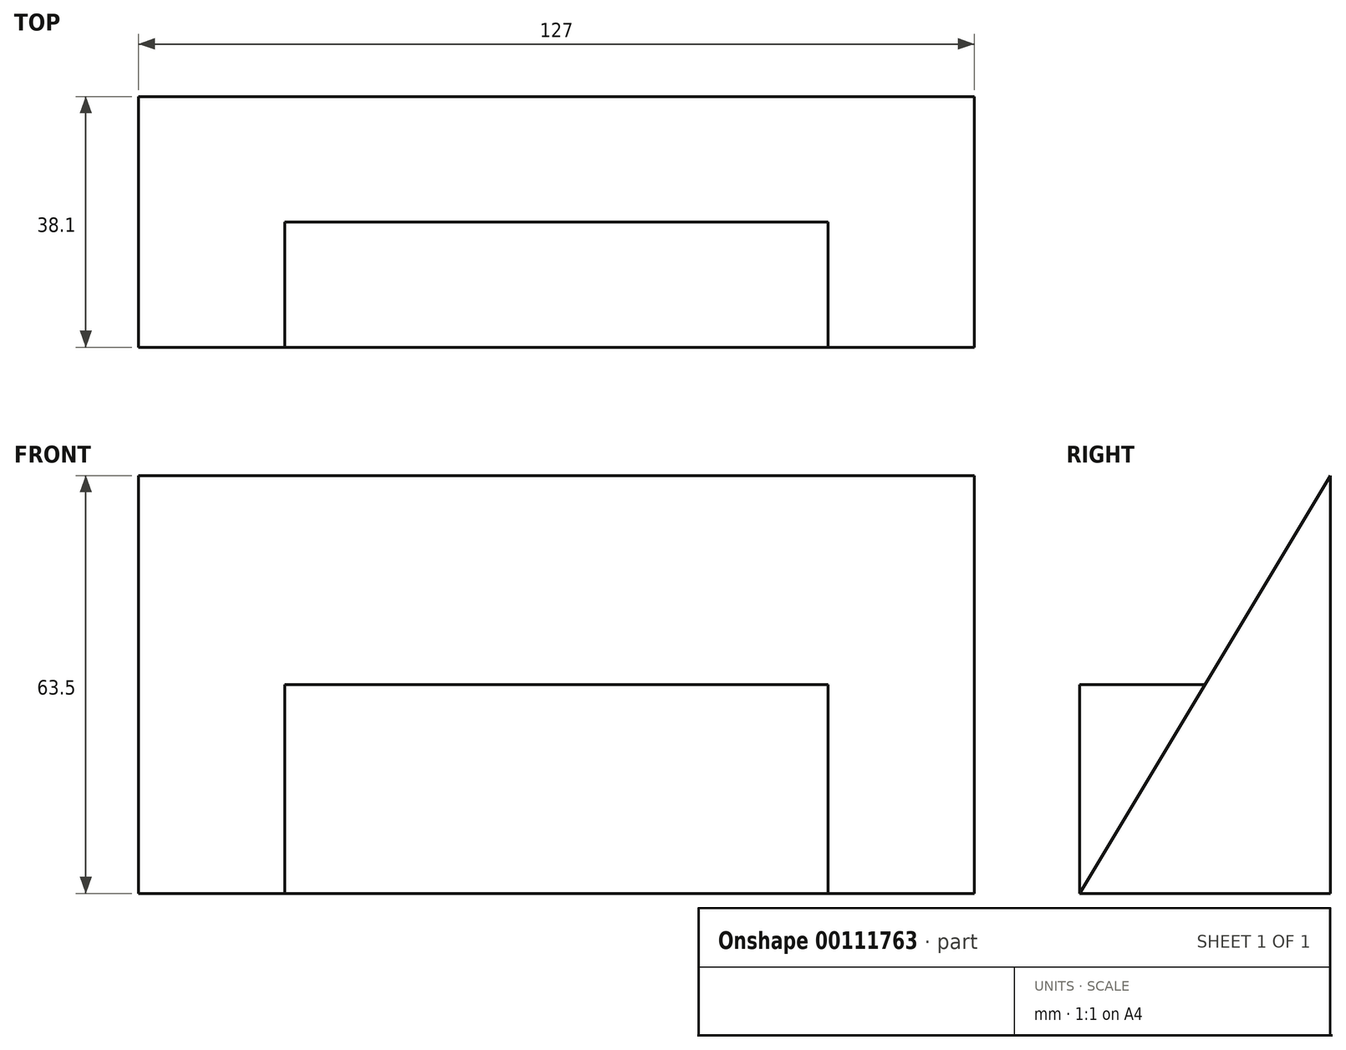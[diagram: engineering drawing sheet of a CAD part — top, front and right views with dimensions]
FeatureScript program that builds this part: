
annotation { "Feature Type Name" : "Feature", "Feature Type Description" : "" }
export const myFeature = defineFeature(function(context is Context, id is Id, definition is map)
    precondition{}
    {
        {
            var Q0;
            Q0=qCreatedBy(makeId("Right.planeOp"),FACE);
            var sketch = newSketch(context, id + "F0", { "sketchPlane" : qUnion([Q0])});
            skLineSegment(sketch, "E0.bottom", {"start": v(-32.56, 28.6) * mm, "end": v(5.54, 28.6) * mm});
            skLineSegment(sketch, "E0.top", {"start": v(-32.56, -34.9) * mm, "end": v(5.54, -34.9) * mm});
            skLineSegment(sketch, "E0.left", {"start": v(-32.56, 28.6) * mm, "end": v(-32.56, -34.9) * mm});
            skLineSegment(sketch, "E0.right", {"start": v(5.54, 28.6) * mm, "end": v(5.54, -34.9) * mm});
            skLineSegment(sketch, "E1", {"start": v(5.54, 28.6) * mm, "end": v(-32.56, -34.9) * mm});
            skLineSegment(sketch, "E2", {"start": v(5.54, -3.15) * mm, "end": v(-32.56, -3.15) * mm});
            skSolve(sketch);
        }
        {
            var Q0;
            Q0=makeQuery(id+"F0.imprint","IMPRINT",FACE,{"disambiguationData":[TD([[makeQuery(id+"F0.imprint","IMPRINT",EDGE,{"derivedFrom":sQuery(id+"F0.wireOp",EDGE,"E0.top")}),1.0]])]});
            var Q1;
            {var subQ1=sQuery(id+"F0.wireOp",EDGE,"E0.right");var subQ3=sQuery(id+"F0.wireOp",EDGE,"E2");var subQ4=makeQuery(id+"F0.imprint","INTERSECT",VERTEX,{"derivedFrom":[subQ1,subQ3]});Q1=makeQuery(id+"F0.imprint","IMPRINT",FACE,{"disambiguationData":[TD([[makeQuery(id+"F0.imprint","IMPRINT",EDGE,{"disambiguationData":[TD([[subQ4,-1.0]])],"derivedFrom":subQ3}),-1.0]])]});}
            var Q2;
            {var subQ1=sQuery(id+"F0.wireOp",EDGE,"E0.left");var subQ3=sQuery(id+"F0.wireOp",EDGE,"E2");var subQ4=makeQuery(id+"F0.imprint","INTERSECT",VERTEX,{"derivedFrom":[subQ1,subQ3]});Q2=makeQuery(id+"F0.imprint","IMPRINT",FACE,{"disambiguationData":[TD([[makeQuery(id+"F0.imprint","IMPRINT",EDGE,{"disambiguationData":[TD([[subQ4,1.0]])],"derivedFrom":subQ3}),1.0]])]});}
            extrude(context, id + "F1", {"entities" : qUnion([Q0, Q1, Q2]), "oppositeDirection" : true, "depth" : 127 * mm});
        }
        {
            var Q0;
            Q0=makeQuery(id+"F1.opExtrude","CAP_FACE",FACE,{"disambiguationData":[OSD([sQuery(id+"F0.wireOp",EDGE,"E0.top"),sQuery(id+"F0.wireOp",EDGE,"E0.left"),sQuery(id+"F0.wireOp",EDGE,"E0.right"),sQuery(id+"F0.wireOp",EDGE,"E1"),sQuery(id+"F0.wireOp",EDGE,"E2")])],"isStart":false});
            var sketch = newSketch(context, id + "F2", { "sketchPlane" : qUnion([Q0])});
            skLineSegment(sketch, "E3", {"start": v(13.51, -3.15) * mm, "end": v(32.56, -34.9) * mm});
            skLineSegment(sketch, "E4", {"start": v(32.56, -34.9) * mm, "end": v(32.56, -3.15) * mm});
            skLineSegment(sketch, "E5", {"start": v(32.56, -3.15) * mm, "end": v(13.51, -3.15) * mm});
            skSolve(sketch);
        }
        {
            var Q0;
            Q0 = qSketchRegion(id + "F2", true);
            extrude(context, id + "F3", {"entities" : qUnion([Q0]), "operationType" : NewBodyOperationType.REMOVE, "oppositeDirection" : true, "depth" : 22.22 * mm});
        }
        {
            var Q0;
            Q0=makeQuery(id+"F1.opExtrude","CAP_FACE",FACE,{"disambiguationData":[OSD([sQuery(id+"F0.wireOp",EDGE,"E0.top"),sQuery(id+"F0.wireOp",EDGE,"E0.left"),sQuery(id+"F0.wireOp",EDGE,"E0.right"),sQuery(id+"F0.wireOp",EDGE,"E1"),sQuery(id+"F0.wireOp",EDGE,"E2")])],"isStart":true});
            var sketch = newSketch(context, id + "F4", { "sketchPlane" : qUnion([Q0])});
            skLineSegment(sketch, "E6", {"start": v(-13.51, -3.15) * mm, "end": v(-32.56, -34.9) * mm});
            skLineSegment(sketch, "E7", {"start": v(-32.56, -34.9) * mm, "end": v(-32.56, -3.15) * mm});
            skLineSegment(sketch, "E8", {"start": v(-32.56, -3.15) * mm, "end": v(-13.51, -3.15) * mm});
            skSolve(sketch);
        }
        {
            var Q0;
            Q0=makeQuery(id+"F4.imprint","IMPRINT",FACE,{"disambiguationData":[TD([[makeQuery(id+"F4.imprint","IMPRINT",EDGE,{"derivedFrom":sQuery(id+"F4.wireOp",EDGE,"E6")}),-1.0]])]});
            extrude(context, id + "F5", {"entities" : qUnion([Q0]), "operationType" : NewBodyOperationType.REMOVE, "oppositeDirection" : true, "depth" : 22.22 * mm});
        }
    });
